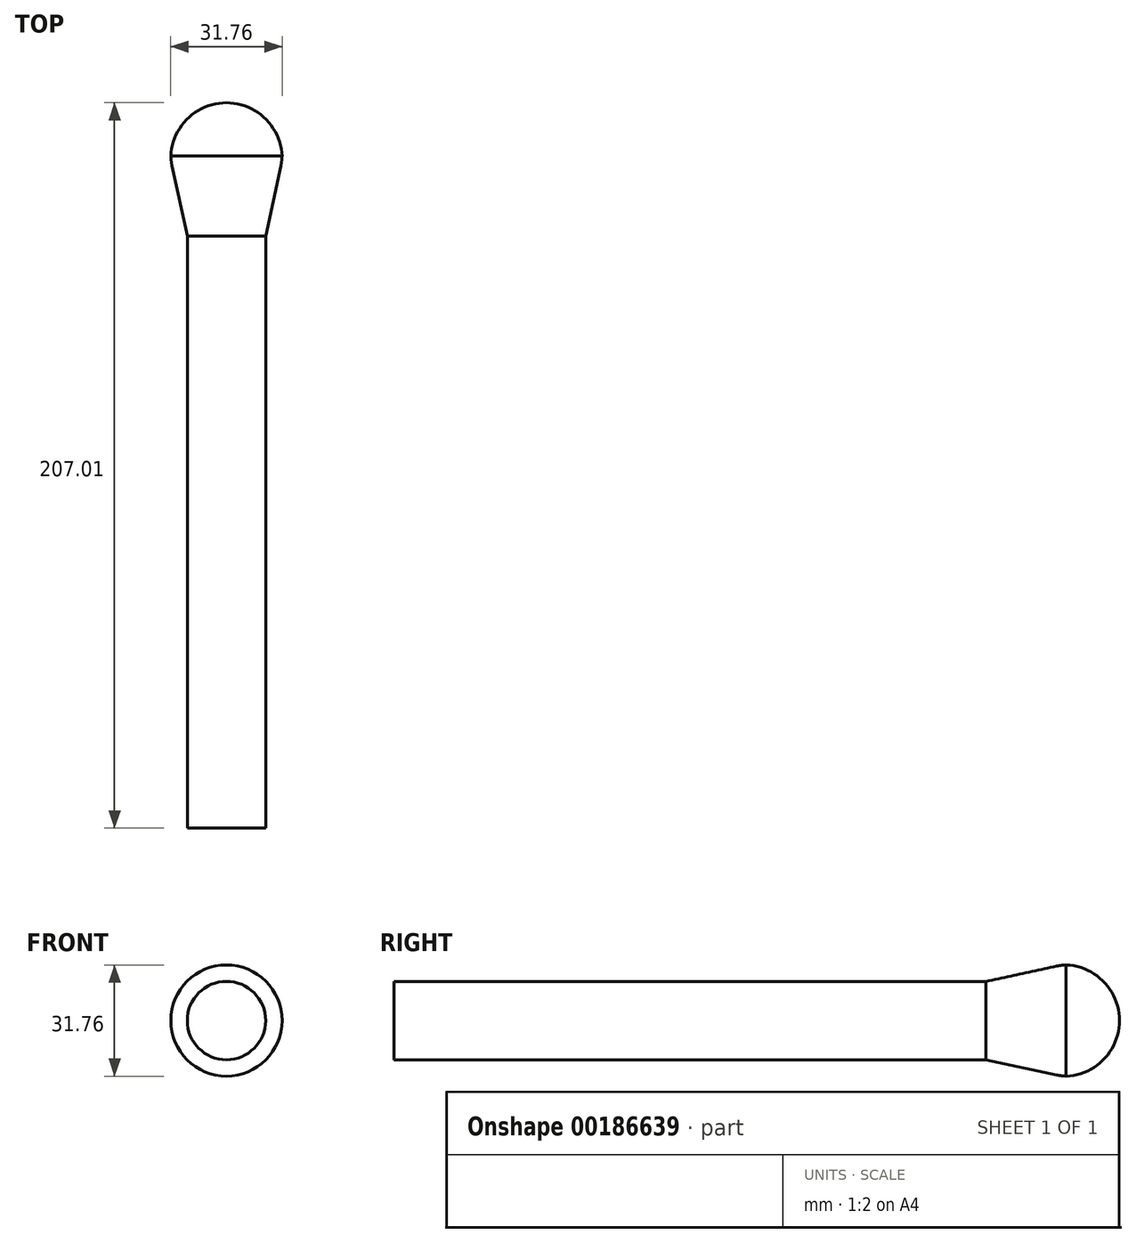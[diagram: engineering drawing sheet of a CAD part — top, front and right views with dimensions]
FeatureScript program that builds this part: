
annotation { "Feature Type Name" : "Feature", "Feature Type Description" : "" }
export const myFeature = defineFeature(function(context is Context, id is Id, definition is map)
    precondition{}
    {
        {
            var Q0;
            Q0=qCreatedBy(makeId("Front.planeOp"),FACE);
            var sketch = newSketch(context, id + "F0", { "sketchPlane" : qUnion([Q0])});
            skCircle(sketch, "E0", {"center": v(0, 0) * mm, "radius": 15.88 * mm});
            skLineSegment(sketch, "E1", {"start": v(0, 0) * mm, "end": v(0, 15.88) * mm, "construction": true});
            skLineSegment(sketch, "E2", {"start": v(0, 0) * mm, "end": v(0, -15.88) * mm, "construction": true});
            skLineSegment(sketch, "E3", {"start": v(0, 0) * mm, "end": v(15.88, 0) * mm, "construction": true});
            skLineSegment(sketch, "E4", {"start": v(0, 0) * mm, "end": v(-15.88, 0) * mm, "construction": true});
            skSolve(sketch);
        }
        {
            var Q0;
            Q0=qCreatedBy(makeId("Right.planeOp"),FACE);
            var sketch = newSketch(context, id + "F1", { "sketchPlane" : qUnion([Q0])});
            skLineSegment(sketch, "E5", {"start": v(0, 0) * mm, "end": v(-22.86, 0) * mm, "construction": true});
            skLineSegment(sketch, "E6", {"start": v(0, 0) * mm, "end": v(15.24, 0) * mm, "construction": true});
            skLineSegment(sketch, "E7", {"start": v(-22.86, 0) * mm, "end": v(15.24, 0) * mm, "construction": true});
            skArc(sketch, "E8", {"start": v(0, -15.88) * mm, "mid": v(15.24, 0) * mm, "end": v(0, 15.88) * mm, "construction": true});
            skLineSegment(sketch, "E9", {"start": v(0, 0) * mm, "end": v(-15.24, 0) * mm, "construction": true});
            skArc(sketch, "E10", {"start": v(0, 15.88) * mm, "mid": v(-15.24, 0) * mm, "end": v(0, -15.88) * mm, "construction": true});
            skLineSegment(sketch, "E11", {"start": v(-22.86, 11.18) * mm, "end": v(-22.86, -11.18) * mm, "construction": true});
            skLineSegment(sketch, "E12", {"start": v(-22.86, 11.18) * mm, "end": v(-2.7, 15.53) * mm, "construction": true});
            skLineSegment(sketch, "E13", {"start": v(-22.86, -11.18) * mm, "end": v(-2.7, -15.53) * mm});
            skArc(sketch, "E14", {"start": v(0, 15.88) * mm, "mid": v(-1.36, 15.76) * mm, "end": v(-2.7, 15.53) * mm, "construction": true});
            skArc(sketch, "E15", {"start": v(-2.7, -15.53) * mm, "mid": v(-1.36, -15.76) * mm, "end": v(0, -15.88) * mm});
            skArc(sketch, "E16", {"start": v(0, -15.88) * mm, "mid": v(10.79, -10.98) * mm, "end": v(15.24, 0) * mm});
            skLineSegment(sketch, "E17", {"start": v(-22.86, 0) * mm, "end": v(-22.86, -11.18) * mm});
            skLineSegment(sketch, "E18", {"start": v(15.24, 0) * mm, "end": v(-22.86, 0) * mm});
            skLineSegment(sketch, "E19.bottom", {"start": v(-22.86, -11.18) * mm, "end": v(-191.77, -11.18) * mm});
            skLineSegment(sketch, "E19.top", {"start": v(-22.86, 11.18) * mm, "end": v(-191.77, 11.18) * mm, "construction": true});
            skLineSegment(sketch, "E19.left", {"start": v(-22.86, -11.18) * mm, "end": v(-22.86, 11.18) * mm});
            skLineSegment(sketch, "E19.right", {"start": v(-191.77, -11.18) * mm, "end": v(-191.77, 0) * mm});
            skLineSegment(sketch, "E20", {"start": v(-22.86, 0) * mm, "end": v(-191.77, 0) * mm});
            skLineSegment(sketch, "E21", {"start": v(-191.77, 11.18) * mm, "end": v(-191.77, 0) * mm, "construction": true});
            skSolve(sketch);
        }
        {
            var Q0;
            {var subQ0=sQuery(id+"F1.wireOp",EDGE,"E19.bottom");Q0=makeQuery(id+"F1.imprint","IMPRINT",FACE,{"disambiguationData":[TD([[makeQuery(id+"F1.imprint","IMPRINT",EDGE,{"derivedFrom":subQ0}),-1.0]])]});}
            var Q1;
            {var subQ2=sQuery(id+"F1.wireOp",EDGE,"E13");Q1=makeQuery(id+"F1.imprint","IMPRINT",FACE,{"disambiguationData":[TD([[makeQuery(id+"F1.imprint","IMPRINT",EDGE,{"derivedFrom":subQ2}),1.0]])]});}
            var Q2;
            Q2=sQuery(id+"F1.wireOp",EDGE,"E20");
            revolve(context, id + "F2", {"entities" : qUnion([Q0, Q1]), "axis" : qUnion([Q2]), "revolveType" : RevolveType.FULL});
        }
    });
